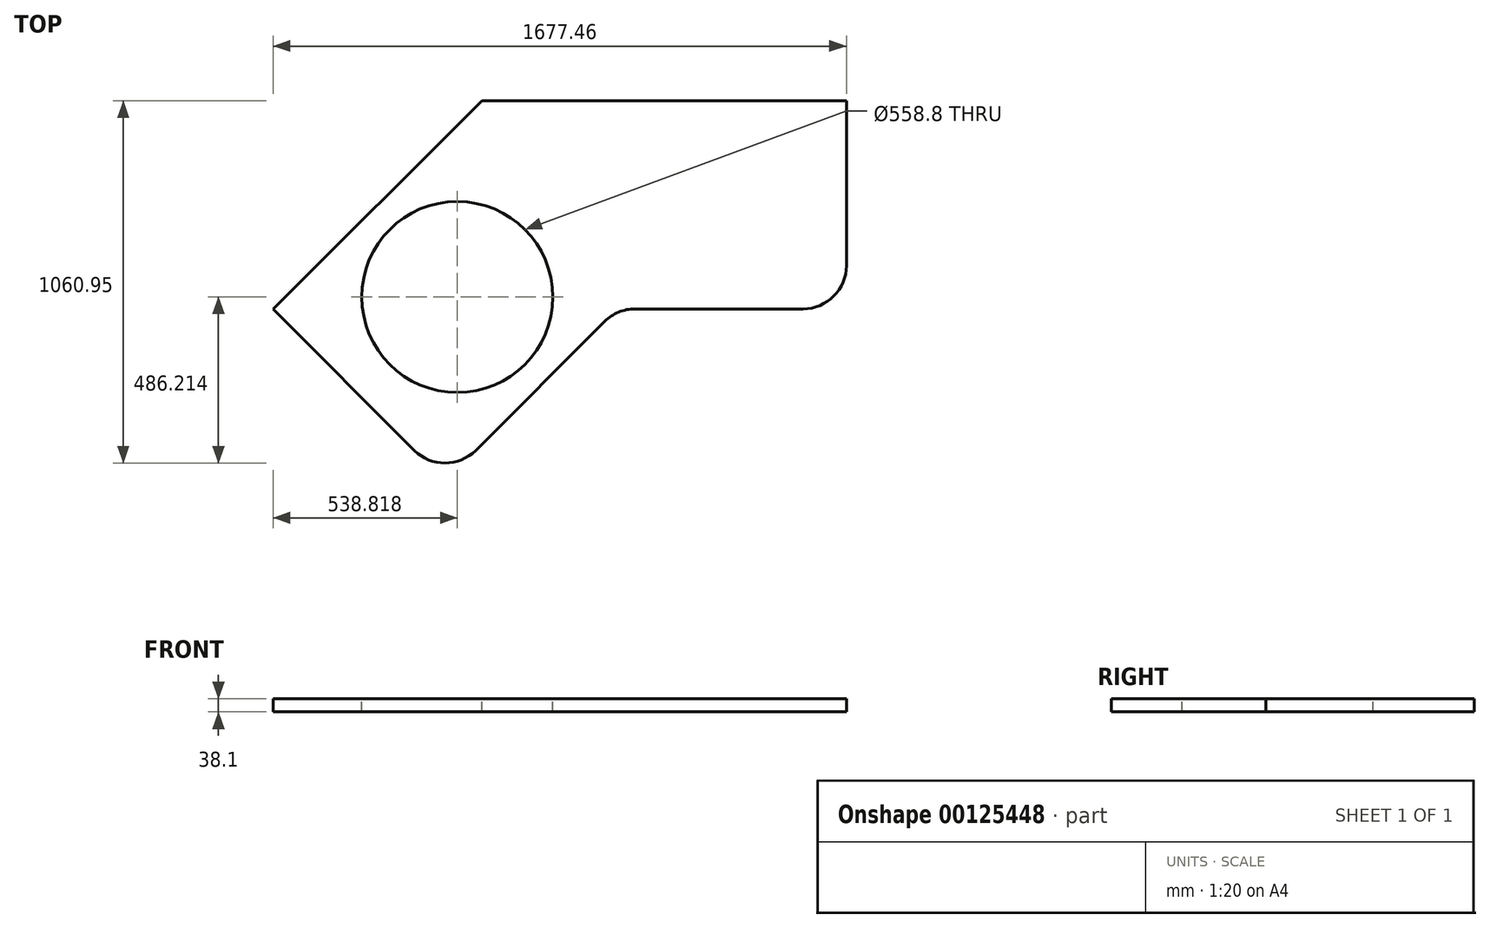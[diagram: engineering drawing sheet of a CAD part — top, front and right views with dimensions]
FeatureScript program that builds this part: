
annotation { "Feature Type Name" : "Feature", "Feature Type Description" : "" }
export const myFeature = defineFeature(function(context is Context, id is Id, definition is map)
    precondition{}
    {
        {
            var Q0;
            Q0=qCreatedBy(makeId("Top.planeOp"),FACE);
            var sketch = newSketch(context, id + "F0", { "sketchPlane" : qUnion([Q0])});
            skLineSegment(sketch, "E0", {"start": v(0, 0) * mm, "end": v(-610.66, -610.66) * mm});
            skLineSegment(sketch, "E1", {"start": v(-610.66, -610.66) * mm, "end": v(-197.57, -1023.75) * mm});
            skLineSegment(sketch, "E2", {"start": v(-17.96, -1023.75) * mm, "end": v(359, -646.8) * mm});
            skLineSegment(sketch, "E3", {"start": v(448.8, -609.6) * mm, "end": v(939.8, -609.6) * mm});
            skLineSegment(sketch, "E4", {"start": v(1066.8, -482.6) * mm, "end": v(1066.8, 0) * mm});
            skLineSegment(sketch, "E5", {"start": v(1066.8, 0) * mm, "end": v(0, 0) * mm});
            skCircle(sketch, "E6", {"center": v(-71.84, -574.74) * mm, "radius": 279.4 * mm});
            skLineSegment(sketch, "E7", {"start": v(-359.21, -862.1) * mm, "end": v(-71.84, -574.74) * mm, "construction": true});
            skPoint(sketch, "E8.visualSharp", {"position": v(-107.76, -1113.55) * mm});
            skArc(sketch, "E8.filletArc", {"start": v(-197.57, -1023.75) * mm, "mid": v(-107.76, -1060.95) * mm, "end": v(-17.96, -1023.75) * mm});
            skPoint(sketch, "E9.visualSharp", {"position": v(396.19, -609.6) * mm});
            skArc(sketch, "E9.filletArc", {"start": v(448.8, -609.6) * mm, "mid": v(400.2, -619.27) * mm, "end": v(359, -646.8) * mm});
            skPoint(sketch, "E10.visualSharp", {"position": v(1066.8, -609.6) * mm});
            skArc(sketch, "E10.filletArc", {"start": v(939.8, -609.6) * mm, "mid": v(1029.6, -572.4) * mm, "end": v(1066.8, -482.6) * mm});
            skLineSegment(sketch, "E11", {"start": v(0, 0) * mm, "end": v(448.8, -736.6) * mm, "construction": true});
            skSolve(sketch);
        }
        {
            var Q0;
            Q0=makeQuery(id+"F0.imprint","IMPRINT",FACE,{"disambiguationData":[TD([[makeQuery(id+"F0.imprint","IMPRINT",EDGE,{"derivedFrom":sQuery(id+"F0.wireOp",EDGE,"E0")}),1.0]])]});
            extrude(context, id + "F1", {"entities" : qUnion([Q0]), "oppositeDirection" : true, "depth" : 38.1 * mm});
        }
    });
